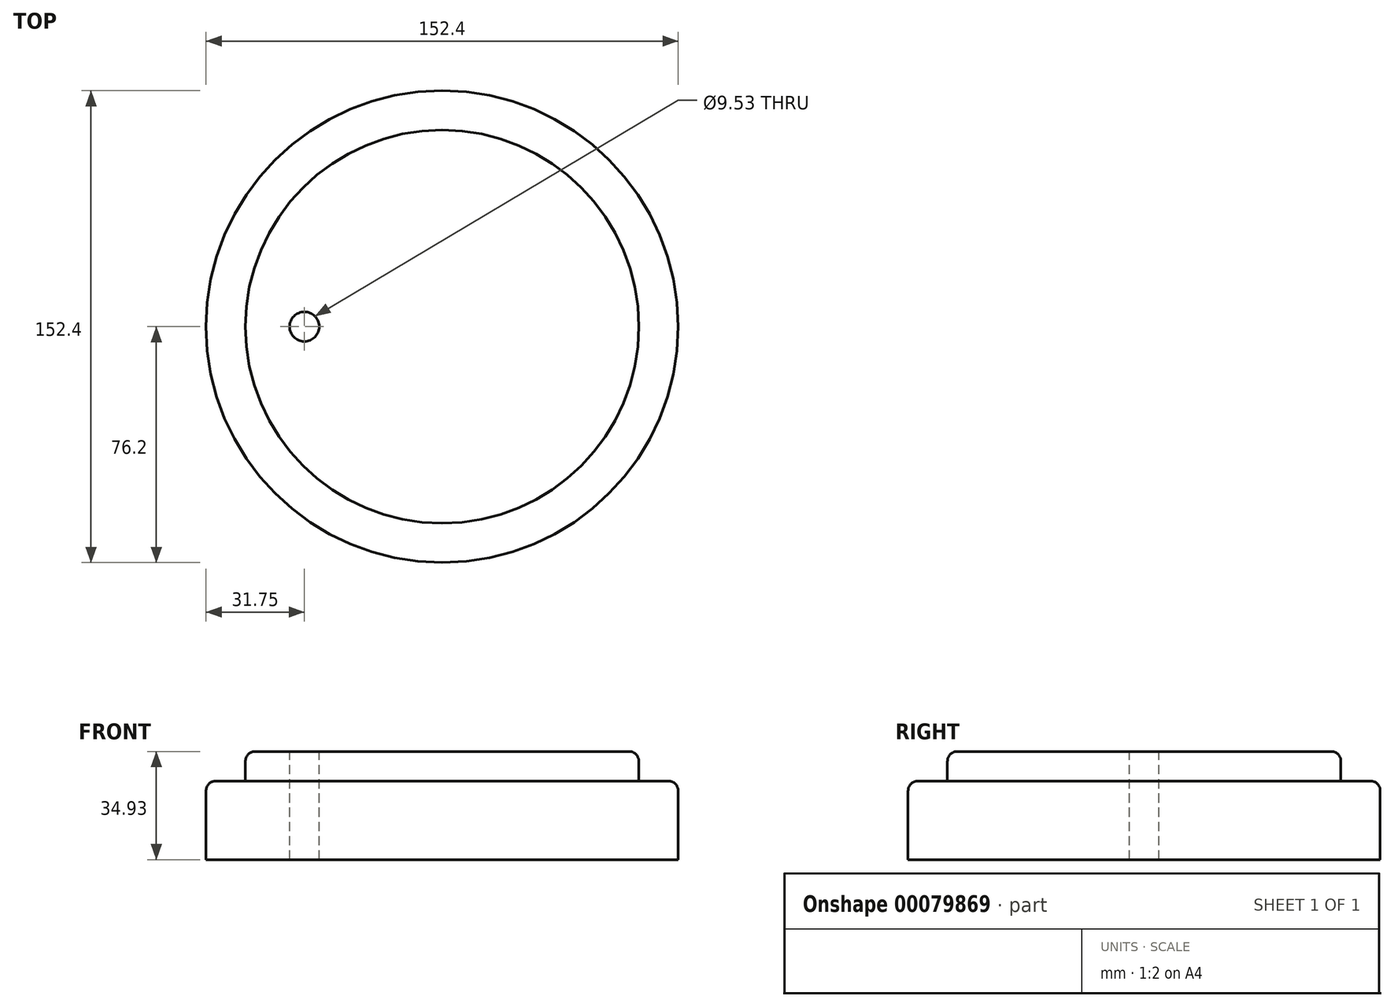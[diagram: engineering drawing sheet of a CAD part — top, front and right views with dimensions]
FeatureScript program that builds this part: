
annotation { "Feature Type Name" : "Feature", "Feature Type Description" : "" }
export const myFeature = defineFeature(function(context is Context, id is Id, definition is map)
    precondition{}
    {
        {
            var Q0;
            Q0=qCreatedBy(makeId("Top.planeOp"),FACE);
            var sketch = newSketch(context, id + "F0", { "sketchPlane" : qUnion([Q0])});
            skCircle(sketch, "E0", {"center": v(0, 0) * mm, "radius": 76.2 * mm});
            skSolve(sketch);
        }
        {
            var Q0;
            Q0=makeQuery(id+"F0.imprint","IMPRINT",FACE,{"disambiguationData":[TD([[makeQuery(id+"F0.imprint","IMPRINT",EDGE,{"derivedFrom":sQuery(id+"F0.wireOp",EDGE,"E0")}),1.0]])]});
            extrude(context, id + "F1", {"entities" : qUnion([Q0]), "depth" : 25.4 * mm});
        }
        {
            var Q0;
            Q0=makeQuery(id+"F1.opExtrude","CAP_FACE",FACE,{"disambiguationData":[OSD([sQuery(id+"F0.wireOp",EDGE,"E0")])],"isStart":false});
            var sketch = newSketch(context, id + "F2", { "sketchPlane" : qUnion([Q0])});
            skCircle(sketch, "E1", {"center": v(0, 0) * mm, "radius": 63.5 * mm});
            skSolve(sketch);
        }
        {
            var Q0;
            Q0=makeQuery(id+"F2.imprint","IMPRINT",FACE,{"disambiguationData":[TD([[makeQuery(id+"F2.imprint","IMPRINT",EDGE,{"derivedFrom":sQuery(id+"F2.wireOp",EDGE,"E1")}),1.0]])]});
            extrude(context, id + "F3", {"entities" : qUnion([Q0]), "operationType" : NewBodyOperationType.ADD, "depth" : 9.53 * mm});
        }
        {
            var Q0;
            Q0=makeQuery(id+"F1.opExtrude","CAP_EDGE",EDGE,{"disambiguationData":[OSD([sQuery(id+"F0.wireOp",EDGE,"E0")])],"isStart":false});
            var Q1;
            Q1=makeQuery(id+"F3.opExtrude","CAP_EDGE",EDGE,{"disambiguationData":[OSD([sQuery(id+"F2.wireOp",EDGE,"E1")])],"isStart":false});
            fillet(context, id + "F4", {"entities" : qUnion([Q0, Q1]), "radius" : 3.17 * mm, "tangentPropagation" : true, "allowEdgeOverflow" : false});
        }
        {
            var Q0;
            Q0=makeQuery(id+"F3.opExtrude","CAP_FACE",FACE,{"disambiguationData":[OSD([sQuery(id+"F2.wireOp",EDGE,"E1")])],"isStart":false});
            var sketch = newSketch(context, id + "F5", { "sketchPlane" : qUnion([Q0])});
            skPoint(sketch, "E2", {"position": v(-44.45, 0) * mm});
            skSolve(sketch);
        }
        {
            var Q0;
            Q0=sQuery(id+"F5.wireOp",VERTEX,"E2");
            var Q1;
            Q1=makeQuery(id+"F1.opExtrude","SWEPT_BODY",BODY,{"disambiguationData":[OSD([sQuery(id+"F0.wireOp",EDGE,"E0")])]});
            hole(context, id + "F6", {"style" : HoleStyle.SIMPLE, "endStyle" : HoleEndStyle.THROUGH, "holeDiameter" : 9.52 * mm, "locations" : qUnion([Q0]), "scope" : qUnion([Q1]), "isTappedThrough" : true});
        }
    });
